# Revit family: NBS_DudleyIndustriesLimited_PprTwlDpnsrs_ModuloSlimlineBehindTheMirrorHandHygieneSystemPaperTowelDispenser
name_source: partatom
category: Specialty Equipment
units: mm (PartAtom-declared; Revit-internal decimal feet)

## family parameters
Always vertical = Yes
Cut with Voids When Loaded = No
Part Type = Normal
Room Calculation Point = No
Round Connector Dimension = Use Diameter
Shared = No
Work Plane-Based = No

## types (1)
- Modulo Slimline Behind The Mirror Hand Hygiene System Paper Towel Dispenser
    Accessories = Not required.,92405BK, Modulo Slimline Base Shelf, 600 mm.,92404BK,  Modulo Slimline Base Shelf, 1200 mm
    AssetType = Fixed
    BIMObjectName = NBS_DudleyIndustriesLimited_PaperTowelDispensers_ModuloSlimlineBehindTheMirrorHandHygieneSystemPaperTowelDispenser
    BlankingPlates = Not required.,Required
    Category = Pr_40_70_22_62:Paper towel dispensers
    Color = Black
    Description = Paper towel dispenser
    Dimensions = 388 x 413 x 173 mm
    DispenserDepth = 173 mm
    DispenserHeight = 413 mm
    DispenserMaterial = NBS_DudleyIndustriesLimited_StainlessSteel_MatteBlackPowderCoated
    DispenserWidth = 388 mm  [stored 1.27297 ft]
    DurationUnit = year
    Finish = Powder-coated
    Form = Wall mounted
    IfcExportAs = IfcFurnitureType
    IfcExportType = NOTDEFINED
    ManufacturerName = Dudley Industries Limited
    ManufacturerURL = www.dudleyindustries.com
    Material = Stainless Steel
    MaterialsBody = Stainless steel
    MaterialsFinishAndColour = Matte black, powder coated
    ModelReference = ModuloSlimlineBehindTheMirrorHandHygieneSystem, PaperTowelDispenser
    NBSCertification = www.nationalbimlibrary.com/cert/c0xm5hfu
    Name = PaperTowelDispensers_ModuloSlimlineBehindTheMirrorHandHygieneSystem, PaperTowelDispenser_DudleyIndustriesLimited
    NominalHeight = 413 mm
    NominalLength = 0 mm  [stored 0 ft]
    NominalWidth = 388 mm  [stored 1.27297 ft]
    Operation = Pull-out
    Shape = Rectangle
    Size = 388 x 413 x 173 mm
    TowelsTowelType = Folded
    TowelsWidth = 250 mm
    Uniclass2015Code = Pr_40_70_22_62
    Uniclass2015Title = Paper towel dispensers
    Uniclass2015Version = Products v1.22
    Version = 1
    WarrantyDescription = Ten year
    WarrantyDurationParts = Ten year
    WarrantyDurationUnit = year

note: [stored X ft] marks values corroborated as IEEE doubles in the binary element streams (Revit-internal decimal feet)

## geometry (parser evidence)
native form markers: Sweep x2
no freeform markers — native parametric forms only
